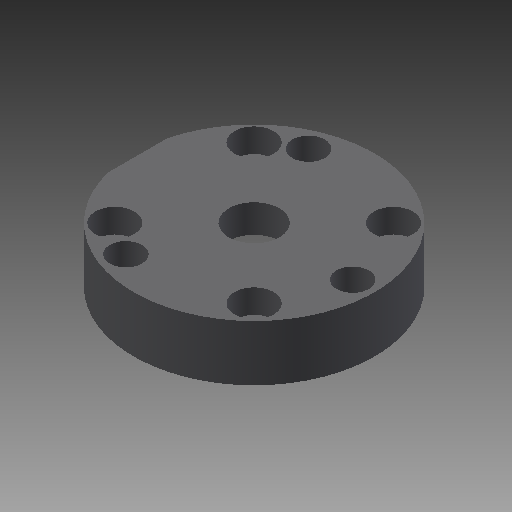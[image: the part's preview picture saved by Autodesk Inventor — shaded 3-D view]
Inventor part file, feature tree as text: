
AUTODESK INVENTOR PART (.ipt)
format: ipt  version: 2017 (Build 210142000, 142)  size: 273,920 bytes
history: native  units: in
note: dims shown in document units (in); Inventor stores cm internally (conversion verified against a paired STEP export)
features: other x287, sketch x10, hole x6, revolve x3, extrude x1, thread x1, pattern_linear x1
ambient origin geometry x8: Origin, YZ Plane, XZ Plane, XY Plane, X Axis, Y Axis, Z Axis, Center Point
bodies: Solid1 (feature_tree)
feature tree (309):
  revolve  "Revolution1"  [1 undecoded]
  extrude  "Extrusion1"  Depth=0.1091in TaperAngle=0.0deg
  revolve  "Revolution2"  Angle=360.0deg
  thread  "Thread1"  [1 undecoded]
  hole  "Hole1"  [1 undecoded]
  hole  "Hole2"  [1 undecoded]
  hole  "Hole3"  [1 undecoded]
  hole  "Hole4"  [1 undecoded]
  hole  "Hole5"  [1 undecoded]
  revolve  "Revolution3"  [1 undecoded]
  hole  "Hole6"  [1 undecoded]
  pattern_linear  "Rectangular Pattern1"  [2 undecoded]
  other  "a1_XY"
  other  "a1_YZ"
  other  "a1_ZX"
  other  "a1_X"
  other  "a1_Y"
  other  "a1_Z"
  other  "a1_Center"
  other  "a2_XY"
  other  "a2_YZ"
  other  "a2_ZX"
  other  "a2_X"
  other  "a2_Y"
  other  "a2_Z"
  other  "a2_Center"
  other  "ar3_XY"
  other  "ar3_YZ"
  other  "ar3_ZX"
  other  "ar3_X"
  other  "ar3_Y"
  other  "ar3_Z"
  other  "ar3_Center"
  other  "ar4_XY"
  other  "ar4_YZ"
  other  "ar4_ZX"
  other  "ar4_X"
  other  "ar4_Y"
  other  "ar4_Z"
  other  "ar4_Center"
  other  "ar5_XY"
  other  "ar5_YZ"
  other  "ar5_ZX"
  other  "ar5_X"
  other  "ar5_Y"
  other  "ar5_Z"
  other  "ar5_Center"
  other  "ar6_XY"
  other  "ar6_YZ"
  other  "ar6_ZX"
  other  "ar6_X"
  other  "ar6_Y"
  other  "ar6_Z"
  other  "ar6_Center"
  other  "b1_XY"
  other  "b1_YZ"
  other  "b1_ZX"
  other  "b1_X"
  other  "b1_Y"
  other  "b1_Z"
  other  "b1_Center"
  other  "c11_XY"
  other  "c11_YZ"
  other  "c11_ZX"
  other  "c11_X"
  other  "c11_Y"
  other  "c11_Z"
  other  "c11_Center"
  other  "c22_XY"
  other  "c22_YZ"
  other  "c22_ZX"
  other  "c22_X"
  other  "c22_Y"
  other  "c22_Z"
  other  "c22_Center"
  other  "d11_XY"
  other  "d11_YZ"
  other  "d11_ZX"
  other  "d11_X"
  other  "d11_Y"
  other  "d11_Z"
  other  "d11_Center"
  other  "d22_XY"
  other  "d22_YZ"
  other  "d22_ZX"
  other  "d22_X"
  other  "d22_Y"
  other  "d22_Z"
  other  "d22_Center"
  other  "j_XY"
  other  "j_YZ"
  other  "j_ZX"
  other  "j_X"
  other  "j_Y"
  other  "j_Z"
  other  "j_Center"
  other  "k1_XY"
  other  "k1_YZ"
  other  "k1_ZX"
  other  "k1_X"
  other  "k1_Y"
  other  "k1_Z"
  other  "k1_Center"
  other  "k2_XY"
  other  "k2_YZ"
  other  "k2_ZX"
  other  "k2_X"
  other  "k2_Y"
  other  "k2_Z"
  other  "k2_Center"
  other  "l1_XY"
  other  "l1_YZ"
  other  "l1_ZX"
  other  "l1_X"
  other  "l1_Y"
  other  "l1_Z"
  other  "l1_Center"
  other  "l2_XY"
  other  "l2_YZ"
  other  "l2_ZX"
  other  "l2_X"
  other  "l2_Y"
  other  "l2_Z"
  other  "l2_Center"
  other  "po1_XY"
  other  "po1_YZ"
  other  "po1_ZX"
  other  "po1_X"
  other  "po1_Y"
  other  "po1_Z"
  other  "po1_Center"
  other  "po2_XY"
  other  "po2_YZ"
  other  "po2_ZX"
  other  "po2_X"
  other  "po2_Y"
  other  "po2_Z"
  other  "po2_Center"
  other  "po3_XY"
  other  "po3_YZ"
  other  "po3_ZX"
  other  "po3_X"
  other  "po3_Y"
  other  "po3_Z"
  other  "po3_Center"
  other  "r7_XY"
  other  "r7_YZ"
  other  "r7_ZX"
  other  "r7_X"
  other  "r7_Y"
  other  "r7_Z"
  other  "r7_Center"
  other  "r71_XY"
  other  "r71_YZ"
  other  "r71_ZX"
  other  "r71_X"
  other  "r71_Y"
  other  "r71_Z"
  other  "r71_Center"
  other  "r72_XY"
  other  "r72_YZ"
  other  "r72_ZX"
  other  "r72_X"
  other  "r72_Y"
  other  "r72_Z"
  other  "r72_Center"
  other  "r73_XY"
  other  "r73_YZ"
  other  "r73_ZX"
  other  "r73_X"
  other  "r73_Y"
  other  "r73_Z"
  other  "r73_Center"
  other  "rg_XY"
  other  "rg_YZ"
  other  "rg_ZX"
  other  "rg_X"
  other  "rg_Y"
  other  "rg_Z"
  other  "rg_Center"
  other  "rh_XY"
  other  "rh_YZ"
  other  "rh_ZX"
  other  "rh_X"
  other  "rh_Y"
  other  "rh_Z"
  other  "rh_Center"
  other  "rs_1_XY"
  other  "rs_1_YZ"
  other  "rs_1_ZX"
  other  "rs_1_X"
  other  "rs_1_Y"
  other  "rs_1_Z"
  other  "rs_1_Center"
  other  "rs_2_XY"
  other  "rs_2_YZ"
  other  "rs_2_ZX"
  other  "rs_2_X"
  other  "rs_2_Y"
  other  "rs_2_Z"
  other  "rs_2_Center"
  other  "rs_3_XY"
  other  "rs_3_YZ"
  other  "rs_3_ZX"
  other  "rs_3_X"
  other  "rs_3_Y"
  other  "rs_3_Z"
  other  "rs_3_Center"
  other  "rs_4_XY"
  other  "rs_4_YZ"
  other  "rs_4_ZX"
  other  "rs_4_X"
  other  "rs_4_Y"
  other  "rs_4_Z"
  other  "rs_4_Center"
  other  "sc1_XY"
  other  "sc1_YZ"
  other  "sc1_ZX"
  other  "sc1_X"
  other  "sc1_Y"
  other  "sc1_Z"
  other  "sc1_Center"
  other  "sc2_XY"
  other  "sc2_YZ"
  other  "sc2_ZX"
  other  "sc2_X"
  other  "sc2_Y"
  other  "sc2_Z"
  other  "sc2_Center"
  other  "sc3_XY"
  other  "sc3_YZ"
  other  "sc3_ZX"
  other  "sc3_X"
  other  "sc3_Y"
  other  "sc3_Z"
  other  "sc3_Center"
  other  "to_dummy_XY"
  other  "to_dummy_YZ"
  other  "to_dummy_ZX"
  other  "to_dummy_X"
  other  "to_dummy_Y"
  other  "to_dummy_Z"
  other  "to_dummy_Center"
  other  "to_nut_XY"
  other  "to_nut_YZ"
  other  "to_nut_ZX"
  other  "to_nut_X"
  other  "to_nut_Y"
  other  "to_nut_Z"
  other  "to_nut_Center"
  other  "to_rod_XY"
  other  "to_rod_YZ"
  other  "to_rod_ZX"
  other  "to_rod_X"
  other  "to_rod_Y"
  other  "to_rod_Z"
  other  "to_rod_Center"
  other  "to_tube_XY"
  other  "to_tube_YZ"
  other  "to_tube_ZX"
  other  "to_tube_X"
  other  "to_tube_Y"
  other  "to_tube_Z"
  other  "to_tube_Center"
  other  "to_wiper_XY"
  other  "to_wiper_YZ"
  other  "to_wiper_ZX"
  other  "to_wiper_X"
  other  "to_wiper_Y"
  other  "to_wiper_Z"
  other  "to_wiper_Center"
  other  "track1_XY"
  other  "track1_YZ"
  other  "track1_ZX"
  other  "track1_X"
  other  "track1_Y"
  other  "track1_Z"
  other  "track1_Center"
  other  "track2_XY"
  other  "track2_YZ"
  other  "track2_ZX"
  other  "track2_X"
  other  "track2_Y"
  other  "track2_Z"
  other  "track2_Center"
  other  "track3_XY"
  other  "track3_YZ"
  other  "track3_ZX"
  other  "track3_X"
  other  "track3_Y"
  other  "track3_Z"
  other  "track3_Center"
  other  "track4_XY"
  other  "track4_YZ"
  other  "track4_ZX"
  other  "track4_X"
  other  "track4_Y"
  other  "track4_Z"
  other  "track4_Center"
  sketch  "Sketch_1"  dims[d0=360.0deg d1=0.344in d2=0.0in]
  sketch  "Sketch_63"
  sketch  "Sketch_37"  dims[d55=0.0in d56=0.0in d57=0.0in d58=0.0in d59=0.0in d60=0.0in d61=0.0in d62=0.0in d63=0.0in d64=0.0in d65=0.0in d66=0.0in d67=0.0in d68=0.0in d69=0.0in d70=0.0in]
  sketch  "Sketch4"  dims[d3=360.0deg d4=0.1091in d5=0.0in]
  sketch  "Sketch5"  dims[d6=0.156in d7=0.75in d8=0.242in d9=0.148in d10=0.5635in d11=0.344in d12=0.0in]
  sketch  "Sketch6"  dims[d13=0.156in d14=0.75in d15=0.242in d16=0.148in d17=0.5635in d18=0.344in d19=0.0in]
  sketch  "Sketch7"  dims[d20=0.156in d21=0.75in d22=0.242in d23=0.148in d24=0.5635in d25=0.344in d26=0.0in]
  sketch  "Sketch8"  dims[d27=0.156in d28=0.75in d29=0.242in d30=0.148in d31=0.5635in d32=0.344in d33=0.0in]
  sketch  "Sketch_9"  dims[d34=0.312in d35=0.75in d36=0.375in d37=0.25in d38=0.5635in d39=0.344in d40=0.0in d41=360.0deg]
  sketch  "Sketch10"  dims[d42=0.1285in d43=0.75in d44=0.2in d45=0.15in d46=0.5635in d47=0.344in d48=0.0in d49=0.7874in d51=1.0098in d52=0.7874in d54=1.0098in]
note: 11 required parameter values undecoded (feature->parameter linkage not recoverable at this tier; creation-order binding heuristic only, values carry confidence <= 0.55)